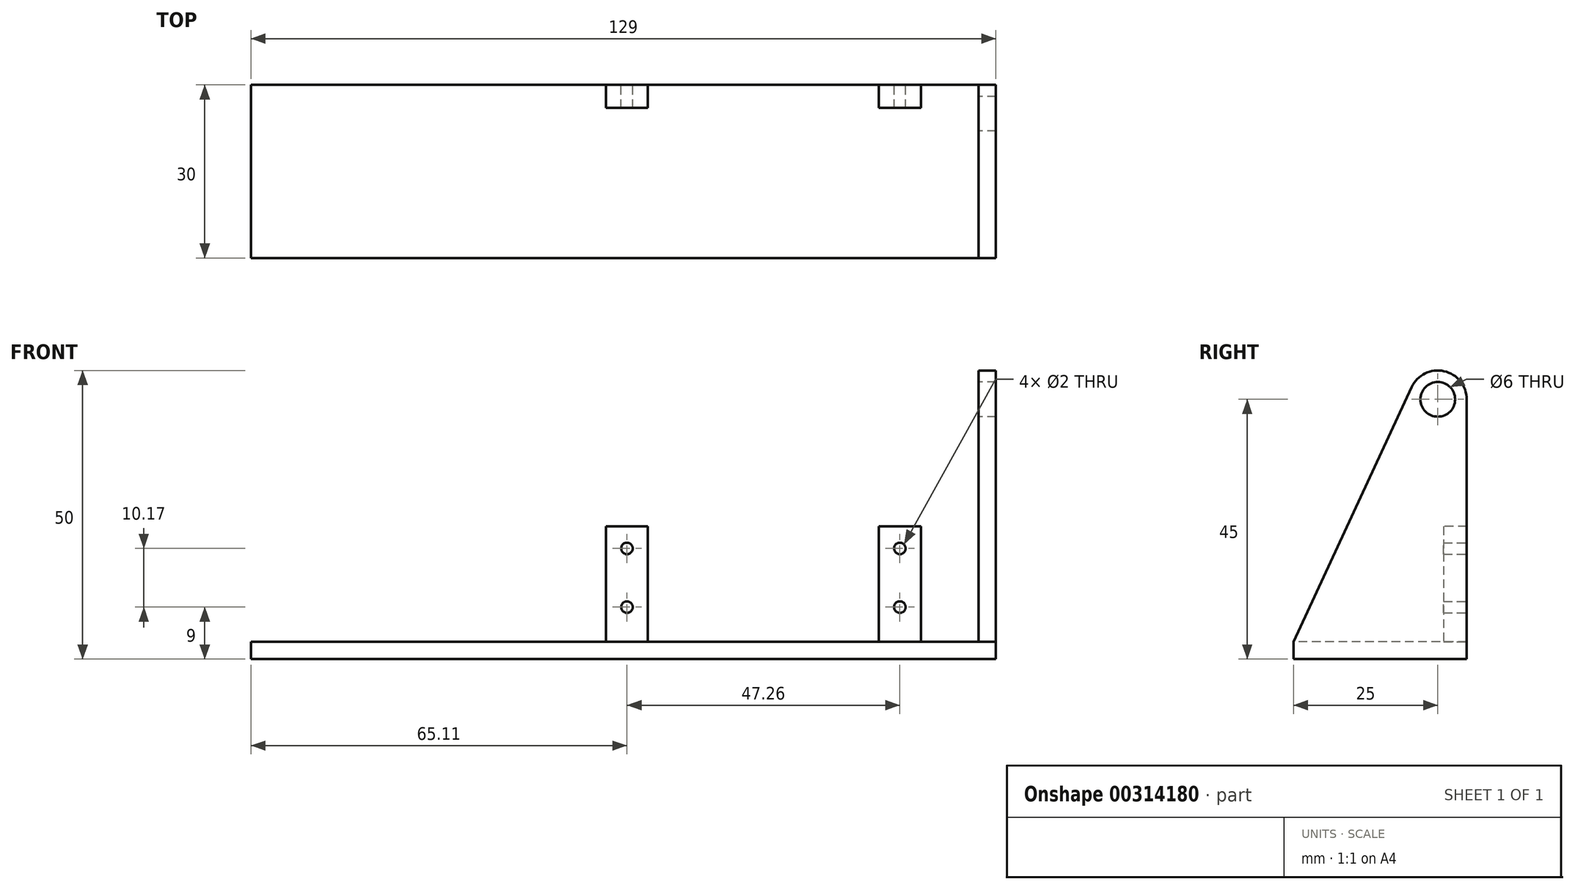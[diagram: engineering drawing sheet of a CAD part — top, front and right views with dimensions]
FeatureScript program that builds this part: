
annotation { "Feature Type Name" : "Feature", "Feature Type Description" : "" }
export const myFeature = defineFeature(function(context is Context, id is Id, definition is map)
    precondition{}
    {
        {
            var Q0;
            Q0=qCreatedBy(makeId("Top.planeOp"),FACE);
            var sketch = newSketch(context, id + "F0", { "sketchPlane" : qUnion([Q0])});
            skLineSegment(sketch, "E0.bottom", {"start": v(-63, 15) * mm, "end": v(63, 15) * mm});
            skLineSegment(sketch, "E0.top", {"start": v(-63, -15) * mm, "end": v(63, -15) * mm});
            skLineSegment(sketch, "E0.left", {"start": v(-63, 15) * mm, "end": v(-63, -15) * mm});
            skLineSegment(sketch, "E0.right", {"start": v(63, 15) * mm, "end": v(63, -15) * mm});
            skPoint(sketch, "E1", {"position": v(0, 15) * mm});
            skPoint(sketch, "E2", {"position": v(63, 0) * mm});
            skSolve(sketch);
        }
        {
            var Q0;
            Q0 = qSketchRegion(id + "F0", true);
            extrude(context, id + "F1", {"entities" : qUnion([Q0]), "depth" : 3 * mm});
        }
        {
            var Q0;
            Q0=makeQuery(id+"F1.opExtrude","SWEPT_FACE",FACE,{"disambiguationData":[OSD([sQuery(id+"F0.wireOp",EDGE,"E0.right")])]});
            var sketch = newSketch(context, id + "F2", { "sketchPlane" : qUnion([Q0])});
            skLineSegment(sketch, "E3.0", {"start": v(15, 3) * mm, "end": v(15, 0) * mm});
            skLineSegment(sketch, "E3.1", {"start": v(15, 0) * mm, "end": v(-15, 0) * mm});
            skLineSegment(sketch, "E3.2", {"start": v(-15, 3) * mm, "end": v(-15, 0) * mm});
            skCircle(sketch, "E4", {"center": v(10, 45) * mm, "radius": 3 * mm});
            skArc(sketch, "E5", {"start": v(15, 45) * mm, "mid": v(11.08, 49.88) * mm, "end": v(5.46, 47.1) * mm});
            skLineSegment(sketch, "E6", {"start": v(-15, 3) * mm, "end": v(5.46, 47.1) * mm});
            skLineSegment(sketch, "E7", {"start": v(15, 45) * mm, "end": v(15, 3) * mm});
            skPoint(sketch, "E8", {"position": v(10, 0) * mm});
            skLineSegment(sketch, "E9", {"start": v(10, -38.17) * mm, "end": v(10, 57.2) * mm, "construction": true});
            skSolve(sketch);
        }
        {
            var Q0;
            Q0=makeQuery(id+"F2.imprint","IMPRINT",FACE,{"disambiguationData":[TD([[makeQuery(id+"F2.imprint","IMPRINT",EDGE,{"derivedFrom":sQuery(id+"F2.wireOp",EDGE,"E4")}),-1.0]])]});
            var Q1;
            Q1=makeQuery(id+"F2.imprint","IMPRINT",FACE,{"disambiguationData":[TD([[makeQuery(id+"F2.imprint","IMPRINT",EDGE,{"derivedFrom":sQuery(id+"F2.wireOp",EDGE,"E3.0")}),-1.0]])]});
            extrude(context, id + "F3", {"entities" : qUnion([Q0, Q1]), "operationType" : NewBodyOperationType.ADD, "depth" : 3 * mm});
        }
        {
            var Q0;
            Q0=makeQuery(id+"F1.opExtrude","CAP_FACE",FACE,{"disambiguationData":[OSD([sQuery(id+"F0.wireOp",EDGE,"E0.bottom"),sQuery(id+"F0.wireOp",EDGE,"E0.top"),sQuery(id+"F0.wireOp",EDGE,"E0.left"),sQuery(id+"F0.wireOp",EDGE,"E0.right")])],"isStart":false});
            var sketch = newSketch(context, id + "F4", { "sketchPlane" : qUnion([Q0])});
            skLineSegment(sketch, "E10", {"start": v(-1.52, 15) * mm, "end": v(5.74, 15) * mm});
            skLineSegment(sketch, "E11", {"start": v(5.74, 15) * mm, "end": v(5.74, 11) * mm});
            skLineSegment(sketch, "E12", {"start": v(-1.52, 11) * mm, "end": v(-1.52, 15) * mm});
            skLineSegment(sketch, "E13", {"start": v(45.74, 15) * mm, "end": v(45.74, 11) * mm});
            skLineSegment(sketch, "E14", {"start": v(53, 11) * mm, "end": v(53, 15) * mm});
            skLineSegment(sketch, "E15", {"start": v(53, 15) * mm, "end": v(45.74, 15) * mm});
            skLineSegment(sketch, "E16", {"start": v(-1.52, 11) * mm, "end": v(5.74, 11) * mm});
            skLineSegment(sketch, "E17", {"start": v(53, 11) * mm, "end": v(45.74, 11) * mm});
            skPoint(sketch, "E18", {"position": v(2.11, 15) * mm});
            skPoint(sketch, "E19", {"position": v(49.37, 15) * mm});
            skSolve(sketch);
        }
        {
            var Q0;
            Q0=makeQuery(id+"F4.imprint","IMPRINT",FACE,{"disambiguationData":[TD([[makeQuery(id+"F4.imprint","IMPRINT",EDGE,{"derivedFrom":sQuery(id+"F4.wireOp",EDGE,"E10")}),-1.0]])]});
            var Q1;
            Q1=makeQuery(id+"F4.imprint","IMPRINT",FACE,{"disambiguationData":[TD([[makeQuery(id+"F4.imprint","IMPRINT",EDGE,{"derivedFrom":sQuery(id+"F4.wireOp",EDGE,"E13")}),1.0]])]});
            extrude(context, id + "F5", {"entities" : qUnion([Q0, Q1]), "operationType" : NewBodyOperationType.ADD, "depth" : 20 * mm});
        }
        {
            var Q0;
            {var subQ0=sQuery(id+"F2.wireOp",EDGE,"E7");var subQ1=sQuery(id+"F2.wireOp",EDGE,"E3.0");Q0=makeQuery(id+"F5.boolean.opBoolean","MERGE",FACE,{"derivedFrom":[makeQuery(id+"Fk4V4EY3QLdC3hS_1.1.F3.boolean.opBoolean","MERGE",FACE,{"derivedFrom":[makeQuery(id+"F3.boolean.opBoolean","MERGE",FACE,{"derivedFrom":[makeQuery(id+"F1.opExtrude","SWEPT_FACE",FACE,{"disambiguationData":[OSD([sQuery(id+"F0.wireOp",EDGE,"E0.bottom")])]}),makeQuery(id+"F3.opExtrude","SWEPT_FACE",FACE,{"disambiguationData":[OSD([subQ1,subQ0])]})]}),makeQuery(id+"Fk4V4EY3QLdC3hS_1.1.F3.opExtrude","SWEPT_FACE",FACE,{"disambiguationData":[OSD([subQ1,subQ0])]})]}),makeQuery(id+"F5.opExtrude","SWEPT_FACE",FACE,{"disambiguationData":[OSD([sQuery(id+"F4.wireOp",EDGE,"E10")])]}),makeQuery(id+"F5.opExtrude","SWEPT_FACE",FACE,{"disambiguationData":[OSD([sQuery(id+"F4.wireOp",EDGE,"E15")])]})]});}
            var sketch = newSketch(context, id + "F6", { "sketchPlane" : qUnion([Q0])});
            skCircle(sketch, "E20", {"center": v(-49.37, 19.17) * mm, "radius": 1 * mm});
            skCircle(sketch, "E21", {"center": v(-2.11, 19.17) * mm, "radius": 1 * mm});
            skCircle(sketch, "E22", {"center": v(-49.37, 9) * mm, "radius": 1 * mm});
            skCircle(sketch, "E23", {"center": v(-2.11, 9) * mm, "radius": 1 * mm});
            skSolve(sketch);
        }
        {
            var Q0;
            Q0=makeQuery(id+"F6.imprint","IMPRINT",FACE,{"disambiguationData":[TD([[makeQuery(id+"F6.imprint","IMPRINT",EDGE,{"derivedFrom":sQuery(id+"F6.wireOp",EDGE,"E20")}),1.0]])]});
            var Q1;
            Q1=makeQuery(id+"F6.imprint","IMPRINT",FACE,{"disambiguationData":[TD([[makeQuery(id+"F6.imprint","IMPRINT",EDGE,{"derivedFrom":sQuery(id+"F6.wireOp",EDGE,"E22")}),1.0]])]});
            var Q2;
            Q2=makeQuery(id+"F6.imprint","IMPRINT",FACE,{"disambiguationData":[TD([[makeQuery(id+"F6.imprint","IMPRINT",EDGE,{"derivedFrom":sQuery(id+"F6.wireOp",EDGE,"E21")}),1.0]])]});
            var Q3;
            Q3=makeQuery(id+"F6.imprint","IMPRINT",FACE,{"disambiguationData":[TD([[makeQuery(id+"F6.imprint","IMPRINT",EDGE,{"derivedFrom":sQuery(id+"F6.wireOp",EDGE,"E23")}),1.0]])]});
            var Q4;
            Q4=makeQuery(id+"F5.opExtrude","SWEPT_FACE",FACE,{"disambiguationData":[OSD([sQuery(id+"F4.wireOp",EDGE,"E17")])]});
            extrude(context, id + "F7", {"entities" : qUnion([Q0, Q1, Q2, Q3]), "operationType" : NewBodyOperationType.REMOVE, "endBound" : BoundingType.UP_TO_SURFACE, "oppositeDirection" : true, "endBoundEntityFace" : qUnion([Q4]), "depth" : 25 * mm});
        }
    });
